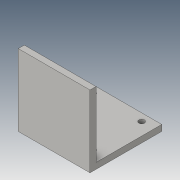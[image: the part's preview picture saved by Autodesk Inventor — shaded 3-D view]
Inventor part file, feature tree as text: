
AUTODESK INVENTOR PART (.ipt)
format: ipt  version: 2016 (Build 200138000, 138)  size: 93,184 bytes
history: native  units: in
note: dims shown in document units (in); Inventor stores cm internally (conversion verified against a paired STEP export)
features: extrude x2, sketch x2, projected_geometry x1
ambient origin geometry x8: Origin, YZ Plane, XZ Plane, XY Plane, X Axis, Y Axis, Z Axis, Center Point
bodies: Solid1 (feature_tree)
feature tree (5):
  extrude  "Extrusion1"  Depth=1.4961in
  extrude  "Extrusion2"  Depth=1.4961in
  sketch  "Sketch1"  dims[d0=0.126in d1=1.4961in]
  sketch  "Sketch2"  dims[d2=0.126in d3=1.4961in d4=1.4961in d5=0.0in d11=0.7874in d13=1.0236in d14=0.7874in d16=1.0236in d19=0.315in d20=0.1181in d21=0.0in d22=0.0in]
  projected_geometry  "Projected Loop1"
